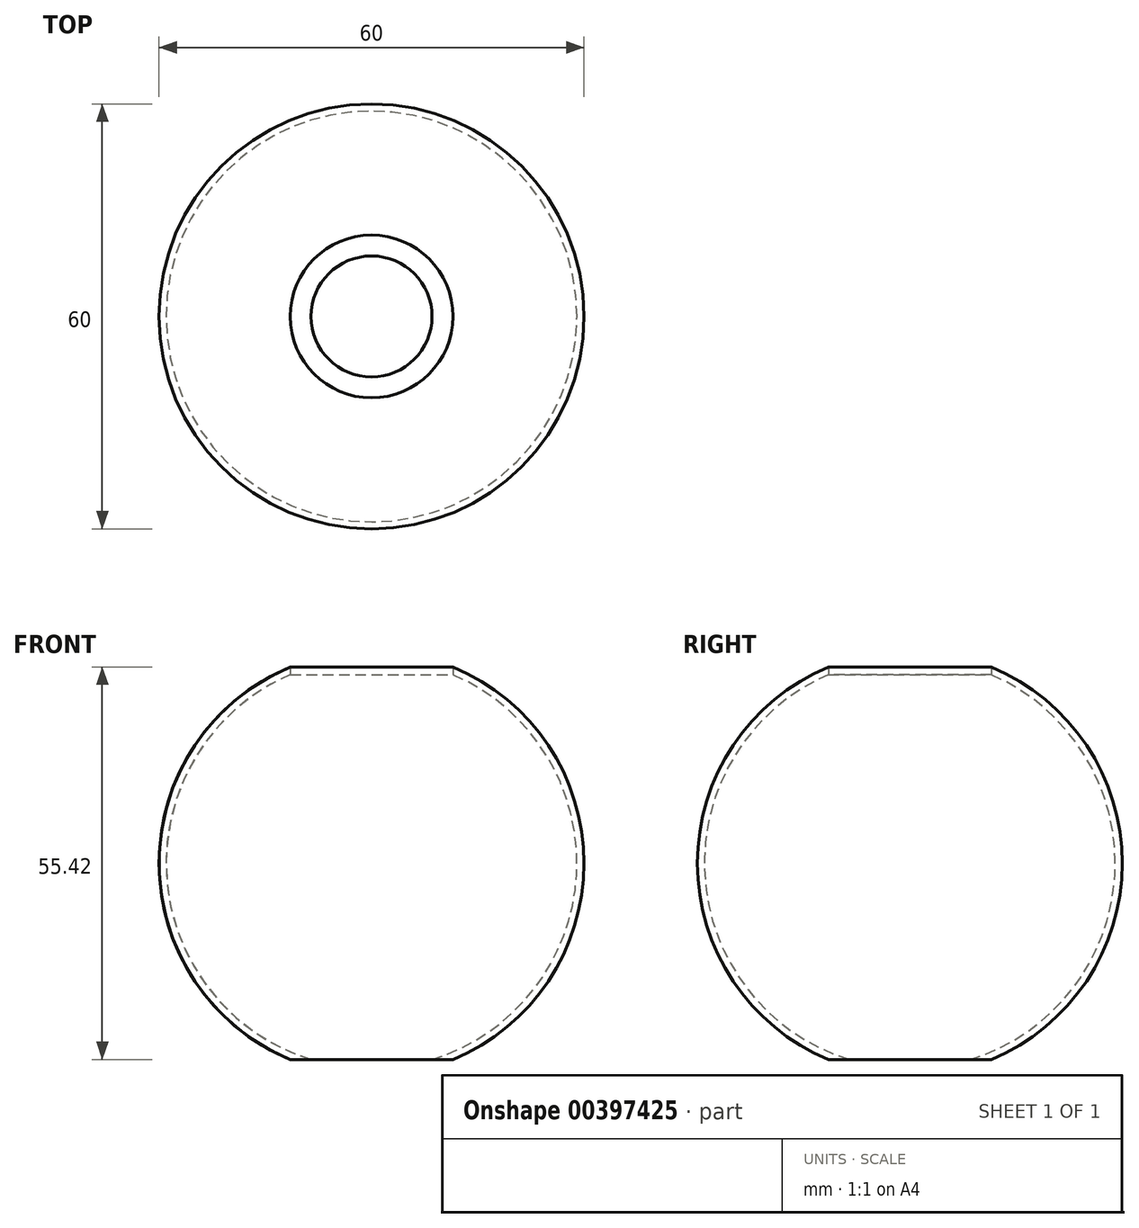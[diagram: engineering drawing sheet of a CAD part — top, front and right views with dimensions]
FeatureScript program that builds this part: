
annotation { "Feature Type Name" : "Feature", "Feature Type Description" : "" }
export const myFeature = defineFeature(function(context is Context, id is Id, definition is map)
    precondition{}
    {
        {
            var Q0;
            Q0=qCreatedBy(makeId("Right.planeOp"),FACE);
            var sketch = newSketch(context, id + "F0", { "sketchPlane" : qUnion([Q0])});
            skArc(sketch, "E0", {"start": v(-11.49, 27.71) * mm, "mid": v(-30, 0) * mm, "end": v(-11.49, -27.71) * mm});
            skArc(sketch, "E1", {"start": v(-11.49, 26.63) * mm, "mid": v(-29, 0) * mm, "end": v(-11.49, -26.63) * mm});
            skLineSegment(sketch, "E2", {"start": v(-11.49, 27.71) * mm, "end": v(-11.49, 26.63) * mm});
            skArc(sketch, "E3", {"start": v(-11.49, -26.63) * mm, "mid": v(-10.03, -27.2) * mm, "end": v(-8.54, -27.71) * mm});
            skLineSegment(sketch, "E4", {"start": v(-11.49, -27.71) * mm, "end": v(-8.54, -27.71) * mm});
            skSolve(sketch);
        }
        {
            var Q0;
            Q0=qCreatedBy(makeId("Right.planeOp"),FACE);
            var sketch = newSketch(context, id + "F1", { "sketchPlane" : qUnion([Q0])});
            skLineSegment(sketch, "E5", {"start": v(0, 0) * mm, "end": v(0, 10) * mm});
            skSolve(sketch);
        }
        {
            var Q0;
            Q0=qSketchRegion(id+"F0",true);
            var Q1;
            Q1=sQuery(id+"F1.wireOp",EDGE,"E5");
            revolve(context, id + "F2", {"entities" : qUnion([Q0]), "axis" : qUnion([Q1]), "revolveType" : RevolveType.FULL});
        }
    });
